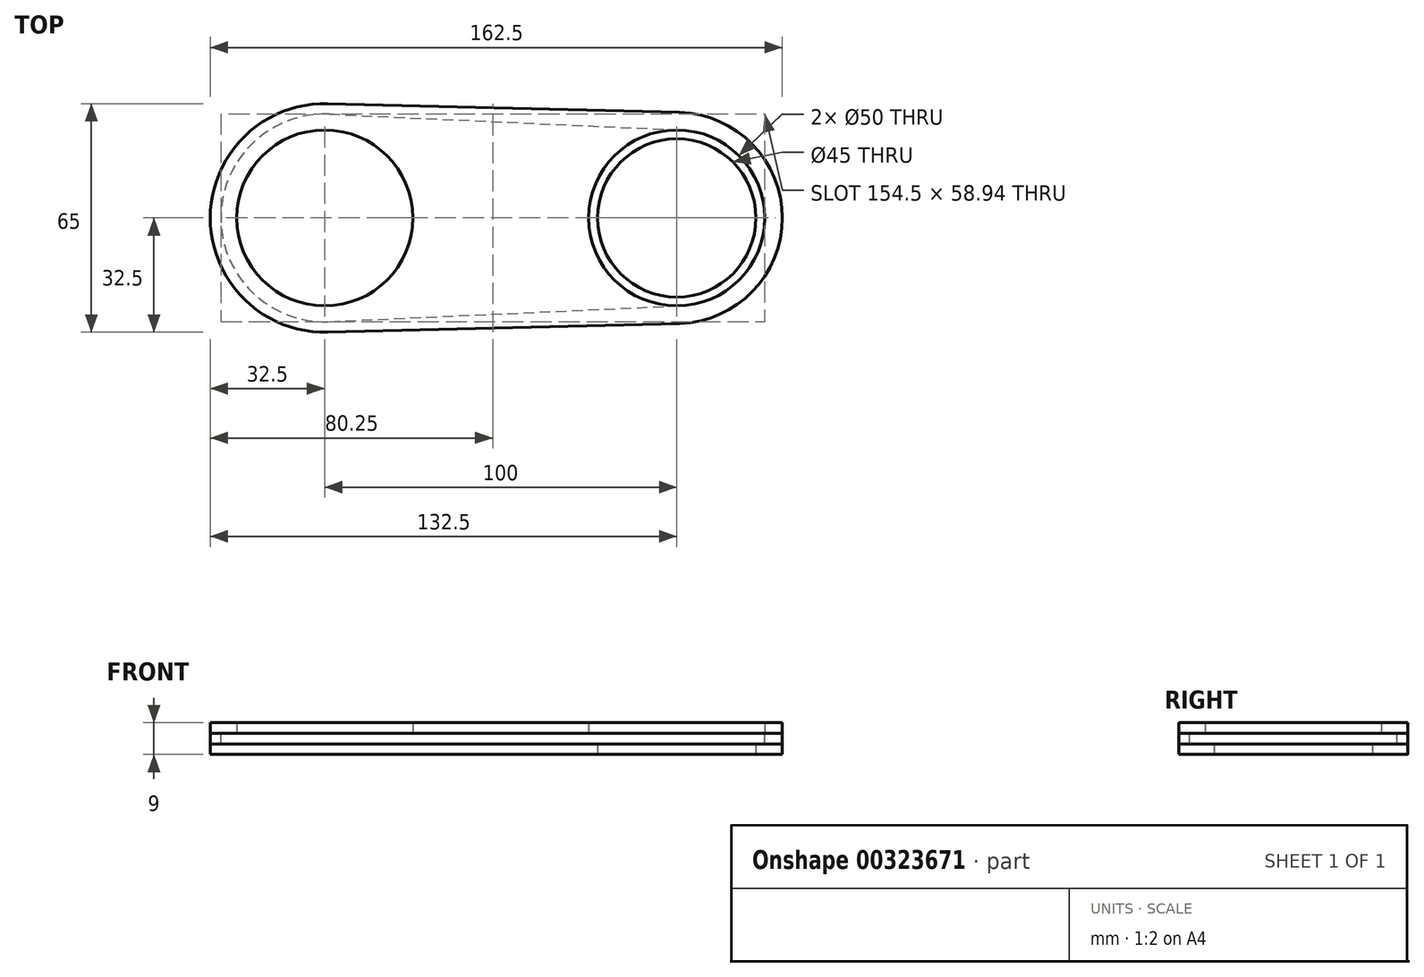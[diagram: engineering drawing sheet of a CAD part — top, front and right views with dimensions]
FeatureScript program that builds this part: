
annotation { "Feature Type Name" : "Feature", "Feature Type Description" : "" }
export const myFeature = defineFeature(function(context is Context, id is Id, definition is map)
    precondition{}
    {
        {
            assignVariable(context, id + "F0", {"name" : "WT", "anyValue" : 3});
        }
        {
            var Q0;
            Q0=qCreatedBy(makeId("Top.planeOp"),FACE);
            var sketch = newSketch(context, id + "F1", { "sketchPlane" : qUnion([Q0])});
            skCircle(sketch, "E0", {"center": v(0, 0) * mm, "radius": 25 * mm});
            skLineSegment(sketch, "E1", {"start": v(0, 0) * mm, "end": v(-100, 0) * mm, "construction": true});
            skArc(sketch, "E2", {"start": v(-86.2, 32.17) * mm, "mid": v(-135, 0) * mm, "end": v(-86.2, -32.17) * mm});
            skArc(sketch, "E3", {"start": v(-99.19, 32.49) * mm, "mid": v(-132.5, 0) * mm, "end": v(-99.19, -32.49) * mm});
            skArc(sketch, "E4", {"start": v(0.75, -30) * mm, "mid": v(30, 0) * mm, "end": v(0.75, 30) * mm});
            skLineSegment(sketch, "E5", {"start": v(-99.19, 32.49) * mm, "end": v(0.75, 30) * mm});
            skLineSegment(sketch, "E6.MirrorCS", {"start": v(-99.19, -32.49) * mm, "end": v(0.75, -30) * mm});
            skCircle(sketch, "E7", {"center": v(-100, 0) * mm, "radius": 25 * mm});
            skSolve(sketch);
        }
        {
            var Q0;
            Q0=qCreatedBy(makeId("Top.planeOp"),FACE);
            var sketch = newSketch(context, id + "F2", { "sketchPlane" : qUnion([Q0])});
            skArc(sketch, "E8.0", {"start": v(-99.19, 32.49) * mm, "mid": v(-132.5, 0) * mm, "end": v(-99.19, -32.49) * mm});
            skLineSegment(sketch, "E8.1", {"start": v(-99.19, 32.49) * mm, "end": v(0.75, 30) * mm});
            skLineSegment(sketch, "E8.2", {"start": v(-99.19, -32.49) * mm, "end": v(0.75, -30) * mm});
            skArc(sketch, "E8.3", {"start": v(0.75, -30) * mm, "mid": v(30, 0) * mm, "end": v(0.75, 30) * mm});
            skCircle(sketch, "E9", {"center": v(-100, 0) * mm, "radius": 29.5 * mm});
            skCircle(sketch, "E10.0", {"center": v(0, 0) * mm, "radius": 25 * mm});
            skLineSegment(sketch, "E11", {"start": v(-98.67, 29.47) * mm, "end": v(1.13, 24.97) * mm});
            skLineSegment(sketch, "E12", {"start": v(-98.67, -29.47) * mm, "end": v(1.13, -24.97) * mm});
            skSolve(sketch);
        }
        {
            var Q0;
            Q0=qCreatedBy(makeId("Top.planeOp"),FACE);
            cPlane(context, id + "F3", {"entities" : qUnion([Q0]), "cplaneType" : CPlaneType.OFFSET, "offset" : (getVariable(context, 'WT') + getVariable(context, 'WT')) * mm, "oppositeDirection" : true, "width" : 150 * mm, "height" : 150 * mm});
        }
        {
            var Q0;
            Q0=qCreatedBy(id+"F3.planeOp",FACE);
            var sketch = newSketch(context, id + "F4", { "sketchPlane" : qUnion([Q0])});
            skArc(sketch, "E13.0", {"start": v(-99.19, 32.49) * mm, "mid": v(-132.5, 0) * mm, "end": v(-99.19, -32.49) * mm});
            skLineSegment(sketch, "E14.0", {"start": v(-99.19, -32.49) * mm, "end": v(0.75, -30) * mm});
            skLineSegment(sketch, "E15.0", {"start": v(-99.19, 32.49) * mm, "end": v(0.75, 30) * mm});
            skArc(sketch, "E16.0", {"start": v(0.75, -30) * mm, "mid": v(30, 0) * mm, "end": v(0.75, 30) * mm});
            skCircle(sketch, "E17", {"center": v(0, 0) * mm, "radius": 22.5 * mm});
            skSolve(sketch);
        }
        {
            var Q0;
            Q0=makeQuery(id+"F1.imprint","IMPRINT",FACE,{"disambiguationData":[TD([[makeQuery(id+"F1.imprint","IMPRINT",EDGE,{"derivedFrom":sQuery(id+"F1.wireOp",EDGE,"E0")}),-1.0]])]});
            extrude(context, id + "F5", {"entities" : qUnion([Q0]), "depth" : (getVariable(context, 'WT')) * mm});
        }
        {
            var Q0;
            Q0=makeQuery(id+"F2.imprint","IMPRINT",FACE,{"disambiguationData":[TD([[makeQuery(id+"F2.imprint","IMPRINT",EDGE,{"derivedFrom":sQuery(id+"F2.wireOp",EDGE,"E8.0")}),1.0]])]});
            extrude(context, id + "F6", {"entities" : qUnion([Q0]), "oppositeDirection" : true, "depth" : (getVariable(context, 'WT')) * mm});
        }
        {
            var Q0;
            Q0=makeQuery(id+"F4.imprint","IMPRINT",FACE,{"disambiguationData":[TD([[makeQuery(id+"F4.imprint","IMPRINT",EDGE,{"derivedFrom":sQuery(id+"F4.wireOp",EDGE,"E13.0")}),1.0]])]});
            extrude(context, id + "F7", {"entities" : qUnion([Q0]), "depth" : (getVariable(context, 'WT')) * mm});
        }
    });
